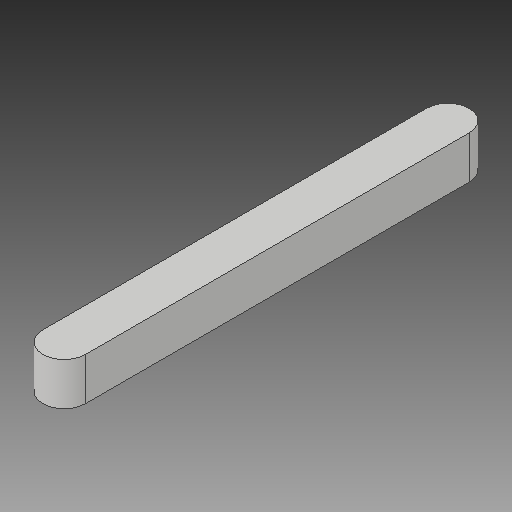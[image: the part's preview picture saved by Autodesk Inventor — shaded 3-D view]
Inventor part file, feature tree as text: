
AUTODESK INVENTOR PART (.ipt)
format: ipt  version: 2019 (Build 230136000, 136)  size: 78,336 bytes
history: native  units: in
note: dims shown in document units (in); Inventor stores cm internally (conversion verified against a paired STEP export)
features: fillet x1
ambient origin geometry x8: Origin, YZ Plane, XZ Plane, XY Plane, X Axis, Y Axis, Z Axis, Center Point
bodies: Solid1 (feature_tree)
feature tree (1):
  fillet  "Fillet1"  [1 undecoded]
note: 1 required parameter value undecoded (feature->parameter linkage not recoverable at this tier; creation-order binding heuristic only, values carry confidence <= 0.55)
